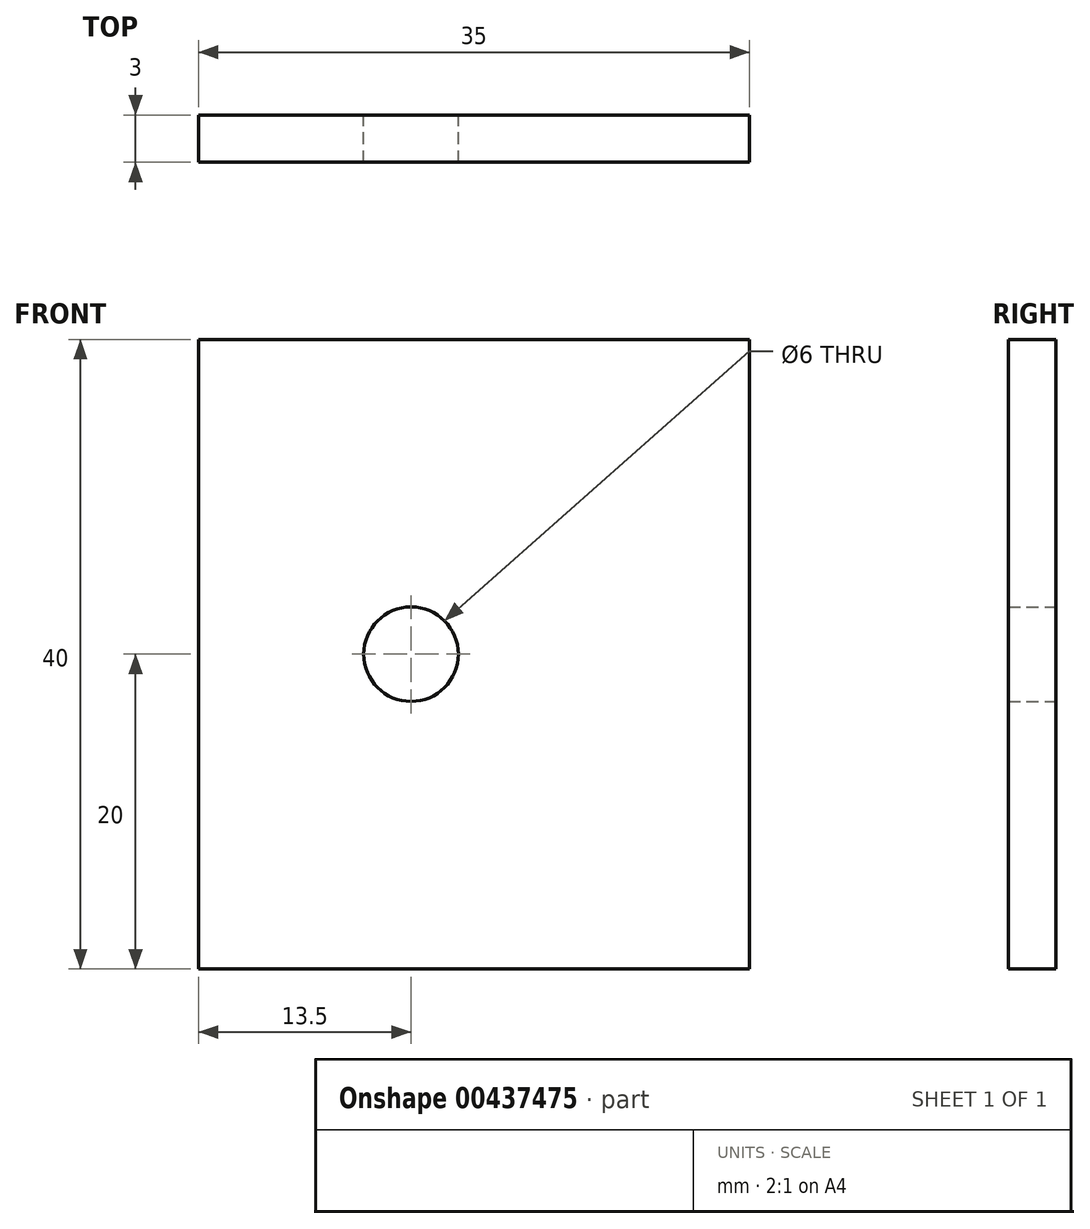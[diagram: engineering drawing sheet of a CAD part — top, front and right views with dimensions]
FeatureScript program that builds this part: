
annotation { "Feature Type Name" : "Feature", "Feature Type Description" : "" }
export const myFeature = defineFeature(function(context is Context, id is Id, definition is map)
    precondition{}
    {
        {
            var Q0;
            Q0=qCreatedBy(makeId("Front.planeOp"),FACE);
            var sketch = newSketch(context, id + "F0", { "sketchPlane" : qUnion([Q0])});
            skLineSegment(sketch, "E0.bottom", {"start": v(17.5, 20) * mm, "end": v(-17.5, 20) * mm});
            skLineSegment(sketch, "E0.top", {"start": v(17.5, -20) * mm, "end": v(-17.5, -20) * mm});
            skLineSegment(sketch, "E0.left", {"start": v(17.5, 20) * mm, "end": v(17.5, -20) * mm});
            skLineSegment(sketch, "E0.right", {"start": v(-17.5, 20) * mm, "end": v(-17.5, -20) * mm});
            skPoint(sketch, "E0.middle", {"position": v(0, 0) * mm});
            skCircle(sketch, "E1", {"center": v(-4, 0) * mm, "radius": 3 * mm});
            skSolve(sketch);
        }
        {
            var Q0;
            Q0 = qSketchRegion(id + "F0", true);
            extrude(context, id + "F1", {"entities" : qUnion([Q0]), "depth" : 3 * mm, "offsetDistance" : 25 * mm});
        }
    });
